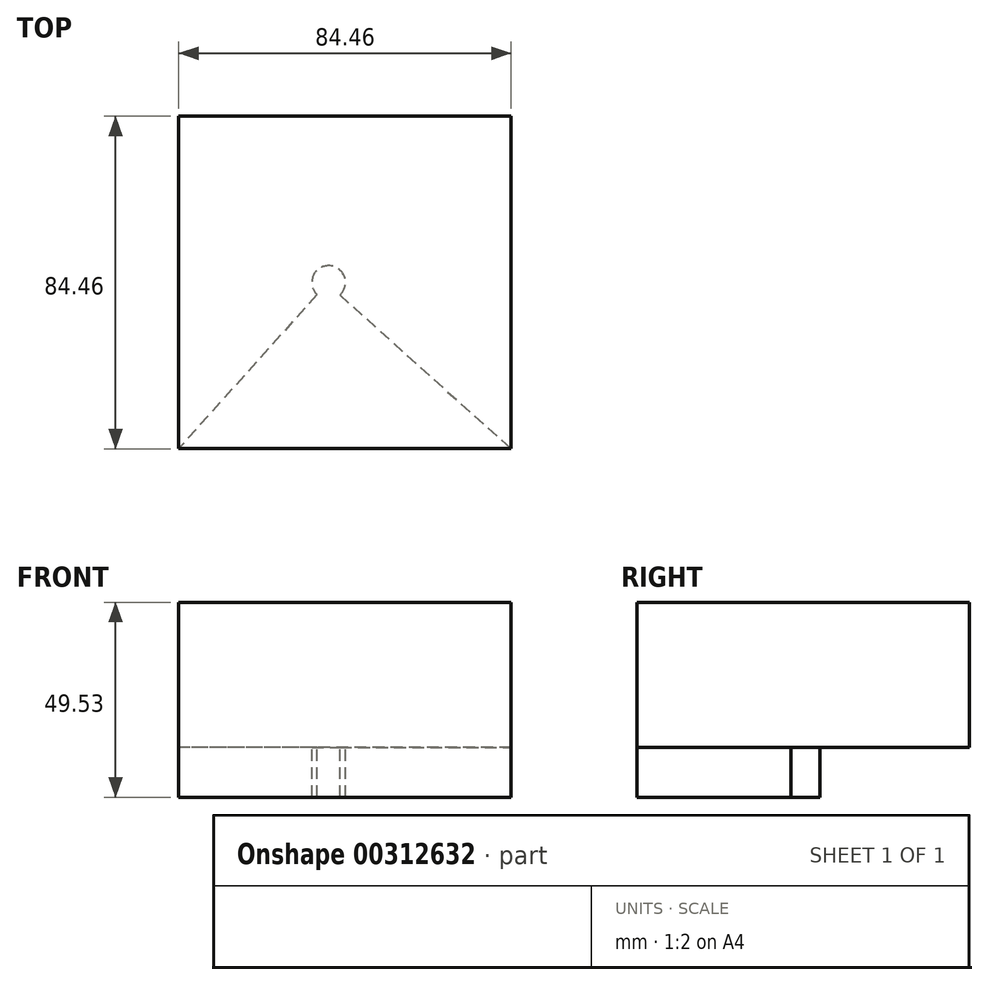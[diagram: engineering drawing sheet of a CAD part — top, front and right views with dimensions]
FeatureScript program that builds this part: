
annotation { "Feature Type Name" : "Feature", "Feature Type Description" : "" }
export const myFeature = defineFeature(function(context is Context, id is Id, definition is map)
    precondition{}
    {
        {
            var Q0;
            Q0=qCreatedBy(makeId("Front.planeOp"),FACE);
            var sketch = newSketch(context, id + "F0", { "sketchPlane" : qUnion([Q0])});
            skLineSegment(sketch, "E0", {"start": v(0, 0) * mm, "end": v(-38.1, 0) * mm});
            skLineSegment(sketch, "E1", {"start": v(-38.1, 0) * mm, "end": v(-38.1, 36.83) * mm});
            skLineSegment(sketch, "E2", {"start": v(-38.1, 36.83) * mm, "end": v(0, 36.83) * mm});
            skLineSegment(sketch, "E3", {"start": v(0, 36.83) * mm, "end": v(46.36, 36.83) * mm});
            skLineSegment(sketch, "E4", {"start": v(46.36, 36.83) * mm, "end": v(46.36, 0) * mm});
            skLineSegment(sketch, "E5", {"start": v(46.36, 0) * mm, "end": v(0, 0) * mm});
            skSolve(sketch);
        }
        {
            var Q0;
            Q0=makeQuery(id+"F0.imprint","IMPRINT",FACE,{"disambiguationData":[TD([[makeQuery(id+"F0.imprint","IMPRINT",EDGE,{"derivedFrom":sQuery(id+"F0.wireOp",EDGE,"E0")}),-1.0]])]});
            extrude(context, id + "F1", {"entities" : qUnion([Q0]), "depth" : 84.45 * mm, "symmetric" : true});
        }
        {
            var Q0;
            Q0=makeQuery(id+"F1.opExtrude","SWEPT_FACE",FACE,{"disambiguationData":[OSD([sQuery(id+"F0.wireOp",EDGE,"E0"),sQuery(id+"F0.wireOp",EDGE,"E5")])]});
            var sketch = newSketch(context, id + "F2", { "sketchPlane" : qUnion([Q0])});
            skLineSegment(sketch, "E6", {"start": v(-38.1, -42.23) * mm, "end": v(-2.97, -2.93) * mm});
            skLineSegment(sketch, "E7", {"start": v(46.36, -42.23) * mm, "end": v(2.82, -3.3) * mm});
            skCircle(sketch, "E8", {"center": v(0, 0) * mm, "radius": 4.28 * mm});
            skLineSegment(sketch, "E9", {"start": v(2.86, 3.18) * mm, "end": v(46.36, 42.23) * mm});
            skLineSegment(sketch, "E10", {"start": v(-2.97, 3.07) * mm, "end": v(-38.1, 42.23) * mm});
            skSolve(sketch);
        }
        {
            var Q0;
            Q0 = qSketchRegion(id + "F2", true);
            var Q1;
            {var subQ0=sQuery(id+"F2.wireOp",EDGE,"E9");Q1=makeQuery(id+"F2.imprint","IMPRINT",FACE,{"disambiguationData":[TD([[makeQuery(id+"F2.imprint","IMPRINT",EDGE,{"derivedFrom":subQ0}),1.0]])]});}
            extrude(context, id + "F3", {"entities" : qUnion([Q0, Q1]), "operationType" : NewBodyOperationType.ADD, "depth" : 12.7 * mm});
        }
    });
